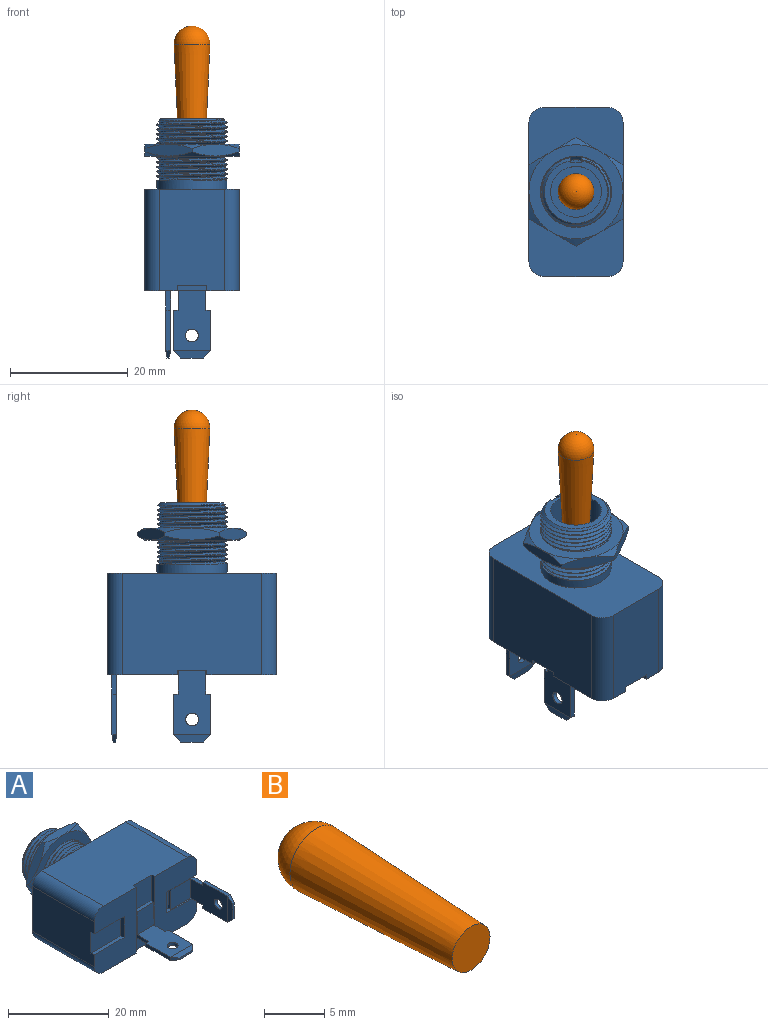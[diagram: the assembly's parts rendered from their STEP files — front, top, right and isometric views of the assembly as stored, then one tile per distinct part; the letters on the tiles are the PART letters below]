
ASSEMBLY  parts=2 mates=1
PART A: 139 faces, bbox 29.5x41.7x19.2 mm
  f0: cylinder r=5.44mm len=1.78mm, axis (0,-1,0), area 1.5mm2, adj f9,f16,f34,f35
  f1: plane 16x16mm, normal (0,1,0), area 86.5mm2, adj f9,f10,f11,f12,f13,f14,f15
  f2: plane 16x16mm, normal (0,-1,0), area 86.5mm2, adj f16,f17,f18,f19,f20,f21,f22
  f3: plane 8.76x5.38mm, normal (0.87,0,-0.5), area 14.2mm2, adj f4,f8,f11,f15,f17,f22
  f4: plane 10.01x2.8mm, normal (0,0,-1), area 14.2mm2, adj f3,f5,f14,f15,f21,f22
  f5: plane 8.76x5.38mm, normal (-0.87,0,-0.5), area 14.2mm2, adj f4,f6,f13,f14,f20,f21
  f6: plane 8.76x5.38mm, normal (-0.87,0,0.5), area 14.2mm2, adj f5,f7,f12,f13,f19,f20
  f7: plane 10.01x2.8mm, normal (0,0,1), area 14.2mm2, adj f6,f8,f10,f12,f18,f19
  f8: plane 8.76x5.38mm, normal (0.87,0,0.5), area 14.2mm2, adj f3,f7,f10,f11,f17,f18
  f9: cone r=6.04mm half-angle=45deg, axis (0,1,0), area 18.2mm2, adj f0,f1,f23,f24,f25,f26,f27,f28
  f10: cone r=9.24mm half-angle=60deg, axis (0,-1,0), area 6.3mm2, adj f1,f7,f8
  f11: cone r=9.24mm half-angle=60deg, axis (0,-1,0), area 6.3mm2, adj f1,f3,f8
  f12: cone r=9.24mm half-angle=60deg, axis (0,-1,0), area 6.3mm2, adj f1,f6,f7
  f13: cone r=9.24mm half-angle=60deg, axis (0,-1,0), area 6.3mm2, adj f1,f5,f6
  f14: cone r=9.24mm half-angle=60deg, axis (0,-1,0), area 6.3mm2, adj f1,f4,f5
  f15: cone r=9.24mm half-angle=60deg, axis (0,-1,0), area 6.3mm2, adj f1,f3,f4
  f16: cone r=5.44mm half-angle=45deg, axis (0,-1,0), area 18.7mm2, adj f0,f2,f29,f30,f31,f32,f33,f34
  f17: cone r=8mm half-angle=60deg, axis (0,1,0), area 6.3mm2, adj f2,f3,f8
  f18: cone r=8mm half-angle=60deg, axis (0,1,0), area 6.3mm2, adj f2,f7,f8
  f19: cone r=8mm half-angle=60deg, axis (0,1,0), area 6.3mm2, adj f2,f6,f7
  f20: cone r=8mm half-angle=60deg, axis (0,1,0), area 6.3mm2, adj f2,f5,f6
  f21: cone r=8mm half-angle=60deg, axis (0,1,0), area 6.3mm2, adj f2,f4,f5
  f22: cone r=8mm half-angle=60deg, axis (0,1,0), area 6.3mm2, adj f2,f3,f4
  f23: cylinder r=5.95mm len=0.9mm, axis (0,1,0), area 0mm2, adj f9,f25,f34
  f24: cylinder r=5.95mm len=11.91mm, axis (0,1,0), area 3.5mm2, adj f9,f27,f34,f35,f112
  f25: bspline ~11.99x11.99mm, area 11.2mm2, adj f9,f23,f34,f35,f101
  f26: bspline ~4.24x2.15mm, area 0mm2, adj f9,f34,f102
  f27: bspline ~11.99x11.99mm, area 20.1mm2, adj f9,f24,f34,f35,f101
  f28: bspline ~6x6mm, area 1.1mm2, adj f9,f34,f102
  f29: cylinder r=5.95mm len=11.87mm, axis (0,1,0), area 2.4mm2, adj f16,f31,f33,f35
  f30: cylinder r=5.44mm len=10.88mm, axis (0,-1,0), area 2.7mm2, adj f16,f31,f32,f35
  f31: bspline ~11.99x11.99mm, area 15.3mm2, adj f16,f29,f30,f35
  f32: bspline ~11.99x11.99mm, area 5.4mm2, adj f16,f30,f35
  f33: bspline ~11.99x11.99mm, area 19.6mm2, adj f16,f29,f34,f35,f103
  f34: plane 10.42x0.95mm, normal (0,0,-1), area 6.8mm2, adj f0,f9,f16,f23,f24,f25,f26,f27
  f35: plane 10.42x0.95mm, normal (0,0,1), area 6.8mm2, adj f0,f9,f16,f24,f25,f27,f29,f30
  f36: plane 10.92x6.35mm, normal (0,0,-1), area 58.9mm2, adj f37,f39,f42,f43,f45,f46,f47,f50
  f37: plane 6.35x4.06mm, normal (1,0,0), area 7.6mm2, adj f36,f38,f40,f41,f46,f52
  f38: plane 4.7x0.79mm, normal (0,0,1), area 3.7mm2, adj f37,f39,f40,f52
  f39: plane 6.35x4.06mm, normal (-1,0,0), area 7.6mm2, adj f36,f38,f40,f41,f42,f52
  f40: plane 5.56x4.7mm, normal (0,-1,0), area 26.1mm2, adj f37,f38,f39,f41
  f41: plane 10.13x6.35mm, normal (0,0,1), area 55.2mm2, adj f37,f39,f40,f42,f43,f45,f46,f47
  f42: plane 0.83x0.79mm, normal (0,1,0), area 0.7mm2, adj f36,f39,f41,f43
  f43: plane 6.86x0.79mm, normal (-1,0,0), area 5.4mm2, adj f36,f41,f42,f49
  f44: plane 3.81x0.41mm, normal (0,-1,0), area 1.6mm2, adj f48,f49,f50,f51
  f45: plane 6.86x0.79mm, normal (1,0,0), area 5.4mm2, adj f36,f41,f46,f48
  f46: plane 0.83x0.79mm, normal (0,1,0), area 0.7mm2, adj f36,f37,f41,f45
  f47: cylinder r=1.09mm len=2.18mm, axis (0,0,-1), area 5.4mm2, adj f36,f41
  f48: plane 1.27x1.27mm, normal (0.71,-0.71,0), area 1.1mm2, adj f44,f45,f50,f51
  f49: plane 1.27x1.27mm, normal (-0.71,-0.71,0), area 1.1mm2, adj f43,f44,f50,f51
  f50: plane 6.35x1.27mm, normal (0,-0.15,-0.99), area 6.5mm2, adj f36,f44,f48,f49
  f51: plane 6.35x1.27mm, normal (0,-0.15,0.99), area 6.5mm2, adj f41,f44,f48,f49
  f52: plane 16x5.08mm, normal (0,-1,0), area 51.5mm2, adj f36,f37,f38,f39,f72,f76,f87,f88
  f53: plane 4.7x0.79mm, normal (-1,0,0), area 3.7mm2, adj f54,f56,f57,f69
  f54: plane 6.35x4.19mm, normal (0,0,-1), area 7.7mm2, adj f53,f55,f57,f58,f59,f69
  f55: plane 11.05x6.35mm, normal (1,0,0), area 59.5mm2, adj f54,f56,f59,f60,f62,f63,f64,f68
  f56: plane 6.35x4.19mm, normal (0,0,1), area 7.7mm2, adj f53,f55,f57,f58,f63,f69
  f57: plane 5.56x4.7mm, normal (0,-1,0), area 26.1mm2, adj f53,f54,f56,f58
  f58: plane 10.26x6.35mm, normal (-1,0,0), area 55.8mm2, adj f54,f56,f57,f59,f60,f62,f63,f64
  f59: plane 0.83x0.79mm, normal (0,1,0), area 0.7mm2, adj f54,f55,f58,f60
  f60: plane 6.86x0.79mm, normal (0,0,-1), area 5.4mm2, adj f55,f58,f59,f65
  f61: plane 3.81x0.41mm, normal (0,-1,0), area 1.6mm2, adj f65,f66,f67,f68
  f62: plane 6.86x0.79mm, normal (0,0,1), area 5.4mm2, adj f55,f58,f63,f66
  f63: plane 0.83x0.79mm, normal (0,1,0), area 0.7mm2, adj f55,f56,f58,f62
  f64: cylinder r=1.09mm len=2.18mm, axis (1,0,0), area 5.4mm2, adj f55,f58
  f65: plane 1.27x1.27mm, normal (0,-0.71,-0.71), area 1.1mm2, adj f60,f61,f67,f68
  f66: plane 1.27x1.27mm, normal (0,-0.71,0.71), area 1.1mm2, adj f61,f62,f67,f68
  f67: plane 6.35x1.27mm, normal (-0.99,-0.15,0), area 6.5mm2, adj f58,f61,f65,f66
  f68: plane 6.35x1.27mm, normal (0.99,-0.15,0), area 6.5mm2, adj f55,f61,f65,f66
  f69: plane 8.38x5.08mm, normal (0,-1,0), area 12.7mm2, adj f53,f54,f55,f56,f78,f84,f85,f86
  f70: plane 16x11.81mm, normal (0,-1,0), area 143.7mm2, adj f71,f72,f76,f77,f78,f84,f85,f86
  f71: cylinder r=2.54mm len=17.27mm, axis (0,1,0), area 68.9mm2, adj f70,f72,f78,f135
  f72: plane 23.62x17.27mm, normal (0,0,1), area 404.1mm2, adj f52,f70,f71,f73,f79,f87,f88,f135
  f73: cylinder r=2.54mm len=17.27mm, axis (0,1,0), area 68.9mm2, adj f72,f74,f79,f135
  f74: plane 17.27x10.92mm, normal (-1,0,0), area 184.1mm2, adj f73,f75,f79,f80,f82,f83,f135
  f75: cylinder r=2.54mm len=17.27mm, axis (0,1,0), area 68.9mm2, adj f74,f76,f79,f135
  f76: plane 23.62x17.27mm, normal (0,0,-1), area 404.1mm2, adj f52,f70,f75,f77,f79,f87,f88,f135
  f77: cylinder r=2.54mm len=17.27mm, axis (0,1,0), area 68.9mm2, adj f70,f76,f78,f135
  f78: plane 17.27x10.92mm, normal (1,0,0), area 184.1mm2, adj f69,f70,f71,f77,f84,f85,f135
  f79: plane 16x11.81mm, normal (0,-1,0), area 143.7mm2, adj f72,f73,f74,f75,f76,f80,f81,f82
  f80: plane 8.38x0.89mm, normal (0,0,-1), area 7.5mm2, adj f74,f79,f81,f83
  f81: plane 5.08x0.89mm, normal (-1,0,0), area 4.5mm2, adj f79,f80,f82,f83
  f82: plane 8.38x0.89mm, normal (0,0,1), area 7.5mm2, adj f74,f79,f81,f83
  f83: plane 8.38x5.08mm, normal (0,-1,0), area 42.6mm2, adj f74,f80,f81,f82
  f84: plane 8.38x0.89mm, normal (0,0,-1), area 7.5mm2, adj f69,f70,f78,f86
  f85: plane 8.38x0.89mm, normal (0,0,1), area 7.5mm2, adj f69,f70,f78,f86
  f86: plane 5.08x0.89mm, normal (1,0,0), area 4.5mm2, adj f69,f70,f84,f85
  f87: plane 16x0.76mm, normal (-1,0,0), area 12.2mm2, adj f52,f70,f72,f76
  f88: plane 16x0.76mm, normal (1,0,0), area 12.2mm2, adj f52,f72,f76,f79
  f89: cylinder r=5.95mm len=11.91mm, axis (0,1,0), area 59mm2, adj f34,f117,f126,f134,f135
  f90: cylinder r=5.95mm len=11.91mm, axis (0,1,0), area 3.5mm2, adj f34,f35,f116,f125
  f91: cylinder r=5.95mm len=11.91mm, axis (0,1,0), area 3.5mm2, adj f34,f35,f115,f124
  f92: cylinder r=5.95mm len=11.91mm, axis (0,1,0), area 3.5mm2, adj f34,f35,f114,f123
  f93: cylinder r=5.95mm len=11.91mm, axis (0,1,0), area 3.5mm2, adj f34,f35,f113,f122
  f94: cylinder r=5.95mm len=11.91mm, axis (0,1,0), area 3.5mm2, adj f34,f35,f111,f121
  f95: cylinder r=5.95mm len=11.91mm, axis (0,1,0), area 3.5mm2, adj f34,f35,f110,f120
  f96: cylinder r=5.95mm len=11.91mm, axis (0,1,0), area 3.5mm2, adj f34,f35,f109,f119
  f97: cylinder r=5.44mm len=10.88mm, axis (0,-1,0), area 3.2mm2, adj f34,f35,f109,f118
  f98: cylinder r=5.44mm len=10.88mm, axis (0,-1,0), area 3.2mm2, adj f34,f35,f110,f119
  f99: cylinder r=5.44mm len=10.88mm, axis (0,-1,0), area 3.2mm2, adj f34,f35,f111,f120
  f100: cylinder r=5.44mm len=10.88mm, axis (0,-1,0), area 3.2mm2, adj f34,f35,f112,f121
  f101: cylinder r=5.44mm len=10.88mm, axis (0,-1,0), area 3.2mm2, adj f25,f27,f34,f35
  f102: cylinder r=5.44mm len=4.26mm, axis (0,-1,0), area 0.4mm2, adj f9,f26,f28,f34
  f103: cylinder r=5.44mm len=10.88mm, axis (0,-1,0), area 3.2mm2, adj f33,f34,f35,f113
  f104: cylinder r=5.44mm len=10.88mm, axis (0,-1,0), area 3.2mm2, adj f34,f35,f114,f122
  f105: cylinder r=5.44mm len=10.88mm, axis (0,-1,0), area 3.2mm2, adj f34,f35,f115,f123
  f106: cylinder r=5.44mm len=10.88mm, axis (0,-1,0), area 3.2mm2, adj f34,f35,f116,f124
  f107: cylinder r=5.44mm len=10.88mm, axis (0,-1,0), area 3.2mm2, adj f34,f35,f117,f125
  f108: cylinder r=5.44mm len=2.83mm, axis (0,-1,0), area 0.1mm2, adj f34,f126,f134
  f109: bspline ~11.99x11.99mm, area 20.2mm2, adj f34,f35,f96,f97
  f110: bspline ~11.99x11.99mm, area 20.2mm2, adj f34,f35,f95,f98
  f111: bspline ~11.99x11.99mm, area 20.2mm2, adj f34,f35,f94,f99
  f112: bspline ~11.99x11.99mm, area 20.2mm2, adj f24,f34,f35,f100
  f113: bspline ~11.99x11.99mm, area 20.2mm2, adj f34,f35,f93,f103
  f114: bspline ~11.99x11.99mm, area 20.2mm2, adj f34,f35,f92,f104
  f115: bspline ~11.99x11.99mm, area 20.2mm2, adj f34,f35,f91,f105
  f116: bspline ~11.99x11.99mm, area 20.2mm2, adj f34,f35,f90,f106
  f117: bspline ~11.99x11.99mm, area 16.6mm2, adj f34,f35,f89,f107,f134
  f118: bspline ~11.99x11.99mm, area 20.1mm2, adj f34,f35,f97,f128,f132
  f119: bspline ~11.99x11.99mm, area 20.2mm2, adj f34,f35,f96,f98
  f120: bspline ~11.99x11.99mm, area 20.2mm2, adj f34,f35,f95,f99
  f121: bspline ~11.99x11.99mm, area 20.2mm2, adj f34,f35,f94,f100
  f122: bspline ~11.99x11.99mm, area 20.2mm2, adj f34,f35,f93,f104
  f123: bspline ~11.99x11.99mm, area 20.2mm2, adj f34,f35,f92,f105
  f124: bspline ~11.99x11.99mm, area 20.2mm2, adj f34,f35,f91,f106
  f125: bspline ~11.99x11.99mm, area 20.2mm2, adj f34,f35,f90,f107
  f126: bspline ~11.99x6mm, area 6.1mm2, adj f34,f89,f108,f134
  f127: cone r=5.35mm half-angle=45deg, axis (0,-1,0), area 13.3mm2, adj f34,f35,f129,f131,f133
  f128: cylinder r=5.95mm len=11.91mm, axis (0,1,0), area 2.9mm2, adj f35,f118,f130,f132
  f129: cylinder r=5.44mm len=10.88mm, axis (0,-1,0), area 3.1mm2, adj f34,f35,f127,f130,f131
  f130: bspline ~11.99x11.99mm, area 18.1mm2, adj f34,f35,f128,f129,f132
  f131: bspline ~11.84x11.84mm, area 7.7mm2, adj f35,f127,f129
  f132: cone r=5.35mm half-angle=45deg, axis (0,-1,0), area 2.5mm2, adj f34,f118,f128,f130
  f133: plane 10.7x10.63mm, normal (0,1,0), area 30.7mm2, adj f34,f35,f127,f136,f138
  f134: plane 12.23x12.23mm, normal (0,1,0), area 10.2mm2, adj f34,f35,f89,f108,f117,f126,f138
  f135: plane 28.7x16mm, normal (0,1,0), area 342.4mm2, adj f71,f72,f73,f74,f75,f76,f77,f78
  f136: cylinder r=4.32mm len=11.94mm, axis (0,1,0), area 323.9mm2, adj f133,f137
  f137: plane 8.64x8.64mm, normal (0,1,0), area 58.6mm2, adj f136
  f138: plane 10.41x1.78mm, normal (1,0,0), area 18.5mm2, adj f34,f35,f133,f134
PART B: 3 faces, bbox 6.1x21.3x6.1 mm
  f0: sphere r=3.05mm, area 61mm2, adj f1
  f1: cone r=3.04mm half-angle=2.6deg, axis (0,1,0), area 300.2mm2, adj f0,f2
  f2: plane 4.43x4.43mm, normal (0,-1,0), area 15.4mm2, adj f1
PLACE A rot(axis=(0.58,0.58,0.58),120deg) t=(35.38,0,-1.29)mm
PLACE B rot(axis=(0.58,0.58,0.58),120deg) t=(35.38,0,0.23)mm
MATE fastened A.f0 <-> B.f1  axis (0,0,1) through (35.38,0,-1.29)mm
